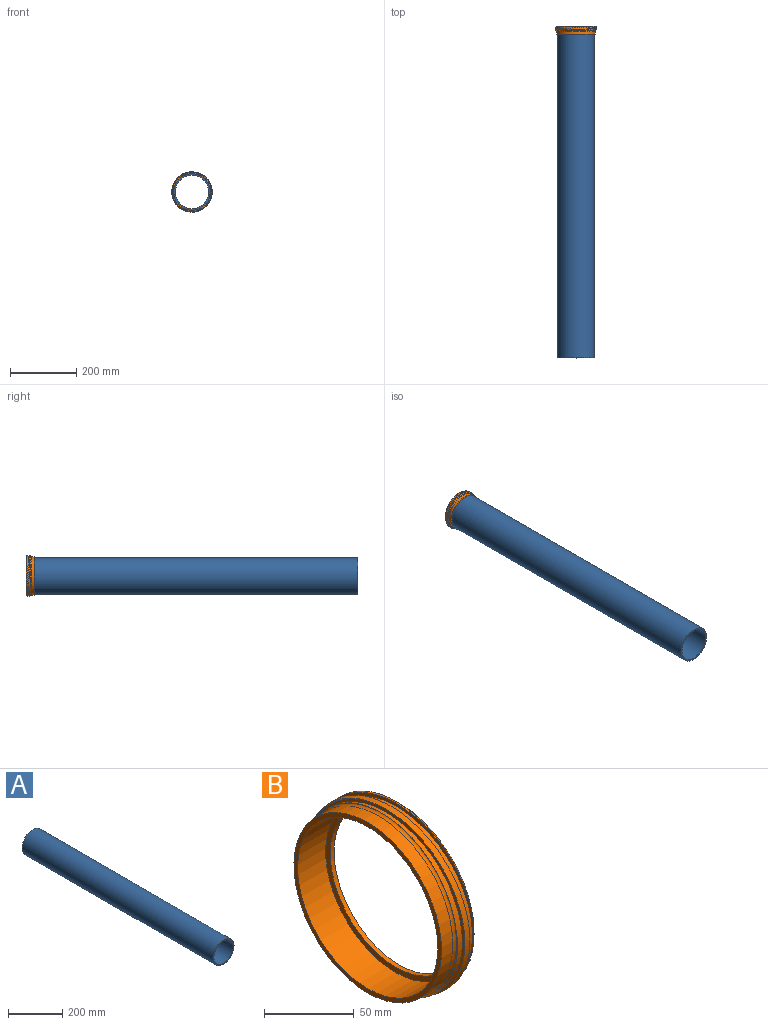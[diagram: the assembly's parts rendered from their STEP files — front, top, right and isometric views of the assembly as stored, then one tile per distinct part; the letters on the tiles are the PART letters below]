
ASSEMBLY  parts=2 mates=1
PART A: 4 faces, bbox 110.2x1000x110.2 mm
  f0: cylinder r=50.1mm len=1000mm, axis (0,1,0), area 314787.6mm2, adj f2,f3
  f1: cylinder r=55.1mm len=1000mm, axis (0,1,0), area 346203.5mm2, adj f2,f3
  f2: plane 110.2x110.2mm, normal (0,-1,0), area 1652.5mm2, adj f0,f1
  f3: plane 110.2x110.2mm, normal (0,1,0), area 1652.5mm2, adj f0,f1
PART B: 14 faces, bbox 25.2x132.1x132.1 mm
  f0: cylinder r=61mm len=122mm, axis (1,0,0), area 1820.4mm2, adj f1,f8,f9,f11,f12
  f1: cone r=61mm half-angle=45deg, axis (1,0,0), area 596.7mm2, adj f0,f10,f11,f12,f13
  f2: cylinder r=58mm len=116mm, axis (1,0,0), area 3191.4mm2, adj f3,f13
  f3: plane 116x116mm, normal (-1,0,0), area 1030.4mm2, adj f2,f4
  f4: cylinder r=55.1mm len=110.2mm, axis (1,0,0), area 7616.5mm2, adj f3,f5
  f5: plane 110.2x110.2mm, normal (-1,0,0), area 1205.6mm2, adj f4,f6
  f6: cylinder r=51.5mm len=103mm, axis (1,0,0), area 970.8mm2, adj f5,f7
  f7: plane 117x117mm, normal (1,0,0), area 2419mm2, adj f6,f9
  f8: cone r=58.5mm half-angle=45deg, axis (-1,0,0), area 134mm2, adj f0,f9,f11
  f9: cone r=58.5mm half-angle=45deg, axis (-1,0,0), area 659.5mm2, adj f0,f7,f8,f10,f12
  f10: cylinder r=59mm len=118mm, axis (-1,0,0), area 2502.4mm2, adj f1,f9,f11,f12
  f11: bspline ~122x122mm, area 1084.2mm2, adj f0,f1,f8,f10
  f12: bspline ~122x122mm, area 1085.4mm2, adj f0,f1,f9,f10
  f13: torus R=61mm, axis (1,0,0), area 863.1mm2, adj f1,f2
PLACE A t=(41.42,-107.21,-87.7)mm
PLACE B rot(axis=(0.58,0.58,0.58),120deg) t=(41.42,-104.21,-87.7)mm
MATE fastened B.f0 <-> A.f1  axis (0,-1,0) through (41.42,-107.21,-87.7)mm
